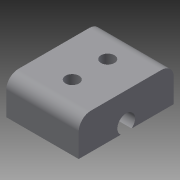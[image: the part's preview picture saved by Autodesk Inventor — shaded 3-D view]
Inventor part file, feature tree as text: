
AUTODESK INVENTOR PART (.ipt)
format: ipt  version: 2015 (Build 190159000, 159)  size: 101,888 bytes
history: native  units: in
note: dims shown in document units (in); Inventor stores cm internally (conversion verified against a paired STEP export)
features: extrude x2, sketch x2, projected_geometry x1
ambient origin geometry x8: Origin, YZ Plane, XZ Plane, XY Plane, X Axis, Y Axis, Z Axis, Center Point
bodies: Solid1 (feature_tree)
feature tree (5):
  extrude  "Extrusion1"  Depth=0.165in
  extrude  "Extrusion2"  Depth=0.125in
  sketch  "Sketch1"  dims[d0=0.184in d1=0.165in]
  sketch  "Sketch2"  dims[d4=0.4in d5=0.125in d6=0.75in d7=0.0in d8=0.14in d9=0.75in d10=0.0in]
  projected_geometry  "Projected Loop1"
